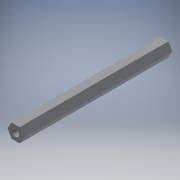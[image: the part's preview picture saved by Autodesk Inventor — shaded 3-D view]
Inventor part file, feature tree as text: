
AUTODESK INVENTOR PART (.ipt)
format: ipt  version: 2017 (Build 210142000, 142)  size: 141,824 bytes
history: native  units: in
note: dims shown in document units (in); Inventor stores cm internally (conversion verified against a paired STEP export)
features: other x4, hole x1, extrude x1, sketch x1, reference x1
ambient origin geometry x8: Origin, YZ Plane, XZ Plane, XY Plane, X Axis, Y Axis, Z Axis, Center Point
bodies: Solid1 (feature_tree)
feature tree (8):
  hole  "Hole1"  [1 undecoded]
  extrude  "Extrusion1"  Depth=1.0in
  sketch  "Sketch1"  dims[d0=0.25in d1=0.25in d2=0.2656in d3=0.75in d4=0.375in d5=0.25in d6=0.5635in d7=20.0in d8=0.8108in d9=1.0in d10=0.0in d11=0.25in]
  reference  "Reference1"
  other  "Default:1"
  parser-record x1  (decoder bookkeeping rows leaked as tree rows — omitted from the tree; the rows remain in map.json)
  other  "SideFrame.iam"
  other  "#35_12T_Sprocket:1"
note: 1 required parameter value undecoded (feature->parameter linkage not recoverable at this tier; creation-order binding heuristic only, values carry confidence <= 0.55)
note: 1 file-system path scrubbed to <path> (originals preserved in map.json)
